# Revit family: 935470001_Sifon Flexible Gris
name_source: partatom
category: Plumbing Fixtures
units: mm (PartAtom-declared; Revit-internal decimal feet)

## family parameters
Always vertical = Yes
Cut with Voids When Loaded = No
OmniClass Number = 23.27.43.00
OmniClass Title = Pipe Fittings
Part Type = Normal
Room Calculation Point = No
Round Connector Dimension = Use Diameter
Shared = No
Work Plane-Based = No

## types (5) — shared parameters
Capacidad de evacuación = 27 lts/min.
Creado por = BIMBAU
Fecha de creación = 09/04/2021
Manufacturer = Grival
Normatividad = NTC 5302.
URL = https://www.grival.com
zero-valued in all types: Default Elevation

## per-type parameters (varying)
| type | Alto | Ciclo de vida de la unidad de cierre | Cuidado Y Limpieza | Description | Diámetro | Longitud | Material | Model | Peso Bruto aprox | Peso Neto aprox | Presion maxima | Recubrimientos | Referencia | Resistencia al torque de roscas plásticas | Temperatura de uso |
| Sifon Flexible Gris Abierto | 38.1 mm  [stored 0.125 ft] |  |  | Para la fabricación de este producto se utilizan materiales, 
equipos y tecnologías de última generación, que permiten 
ofrecer un artículo con los más altos estándares de calidad. | 38.1 mm  [stored 0.125 ft] | 860 mm  [stored 2.82152 ft] | Corona_Plastico_Gris |  |  |  | 34 k Pa (5 psi). | -Resistente a la corrosión, pelado y decoloración por agua. -Resistente al efecto de jabones y limpiadores de tocador. -Recubrimientos no tóxicos. -Condición de servicio recomendada, uso doméstico | 935470001 | mínimo 2 0 N-m (15 Lb-pie). | De 4º C a 66º C (40º F y 150º F). |
| Sifon Flexible Gris Cerrado | 38.1 mm  [stored 0.125 ft] |  |  | Para la fabricación de este producto se utilizan materiales, 
equipos y tecnologías de última generación, que permiten 
ofrecer un artículo con los más altos estándares de calidad. | 38.1 mm  [stored 0.125 ft] | 370 mm  [stored 1.21391 ft] | Corona_Plastico_Gris |  |  |  | 34 k Pa (5 psi). | -Resistente a la corrosión, pelado y decoloración por agua. -Resistente al efecto de jabones y limpiadores de tocador. -Recubrimientos no tóxicos. -Condición de servicio recomendada, uso doméstico | 935470001 | mínimo 2 0 N-m (15 Lb-pie). | De 4º C a 66º C (40º F y 150º F). |
| Sifon Flexible Metalizado Abierto | 38.1 mm  [stored 0.125 ft] |  |  | Para la fabricación de este producto se utilizan materiales, 
equipos y tecnologías de última generación, que permiten 
ofrecer un artículo con los más altos estándares de calidad. | 38.1 mm  [stored 0.125 ft] | 680 mm  [stored 2.23097 ft] | Corona_Plastico_Cromado |  |  |  | 34 k Pa (5 psi). | -Resistente a la corrosión, pelado y decoloración por agua. -Resistente al efecto de jabones y limpiadores de tocador. -Recubrimientos no tóxicos. -Condición de servicio recomendada, uso doméstico | 935490001 | mínimo 2 0 N-m (15 Lb-pie). | De 4º C a 66º C (40º F y 150º F). |
| Sifon Flexible Metalizado Cerrado | 38.1 mm  [stored 0.125 ft] |  |  | Para la fabricación de este producto se utilizan materiales, 
equipos y tecnologías de última generación, que permiten 
ofrecer un artículo con los más altos estándares de calidad. | 38.1 mm  [stored 0.125 ft] | 320 mm  [stored 1.04987 ft] | Corona_Plastico_Cromado |  |  |  | 34 k Pa (5 psi). | -Resistente a la corrosión, pelado y decoloración por agua. -Resistente al efecto de jabones y limpiadores de tocador. -Recubrimientos no tóxicos. -Condición de servicio recomendada, uso doméstico | 935490001 | mínimo 2 0 N-m (15 Lb-pie). | De 4º C a 66º C (40º F y 150º F). |
| Sifon Botella Flexible Gris | 155.9 mm  [stored 0.511483 ft] | 500.000 ciclos. | Los acabados superficiales son aquellos que le imprimen una 
apariencia especial y estética a su producto y además le brindan 
protección. Para prolongar sus cualidades es vital que la limpieza 
profunda del producto se haga únicamente con agua y jabón 
suave y que en el secado y el brillo se utilice un paño de algodón 
limpio; dicha limpieza se recomienda 2 veces a la semana y en 
zonas costeras a diario por la salinidad del ambiente. Por ningún 
motivo deben usarse elementos abrasivos, ácidos o disolventes 
para la limpieza del producto. Los acabados pueden variar su 
comportamiento en zonas costeras y/o en ambientes corrosivos. | -Material en plastico de alta resistencia y duralibilidad. -Fácil proceso de instalación. -Funciona para doble poceta. | 65.4 mm  [stored 0.214567 ft] | 579 mm  [stored 1.89961 ft] | Corona_Plastico_Gris | Sifon Botella Flexible Gris x6 | 340gr. - 0,75lb. | 300gr. - 0,66lb. |  |  | 937633331 |  |  |

type visibility flags: 5 boolean params named "<type name>" — each type sets only its own to Yes (folded from table)

note: [stored X ft] marks values corroborated as IEEE doubles in the binary element streams (Revit-internal decimal feet)

## geometry (parser evidence)
native form markers: Sweep x13
no freeform markers — native parametric forms only
